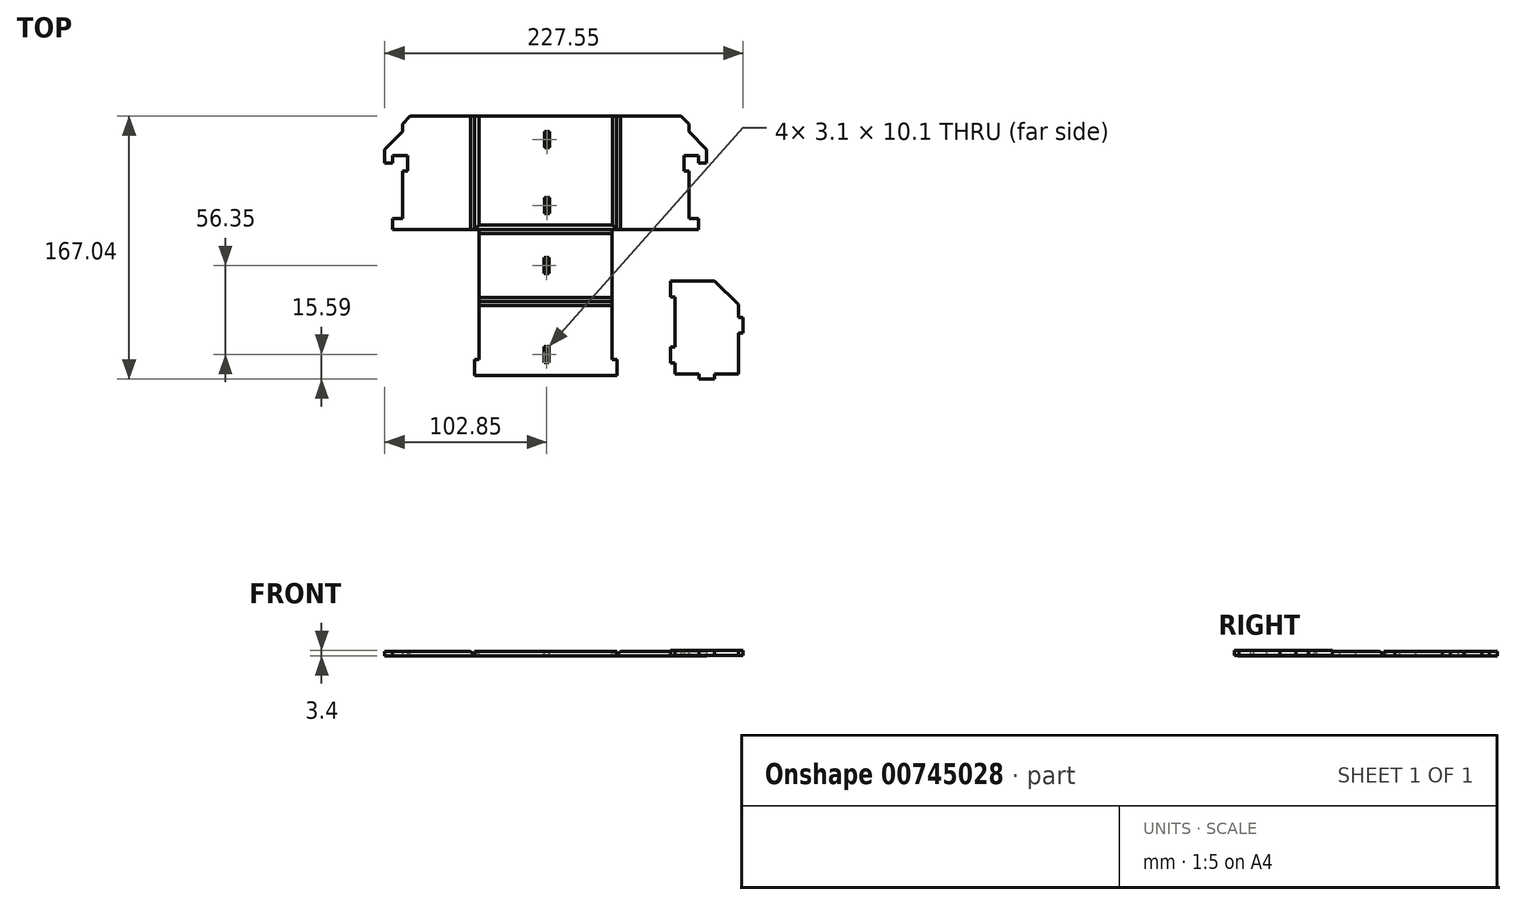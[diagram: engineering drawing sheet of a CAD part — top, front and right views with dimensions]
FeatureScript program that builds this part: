
annotation { "Feature Type Name" : "Feature", "Feature Type Description" : "" }
export const myFeature = defineFeature(function(context is Context, id is Id, definition is map)
    precondition{}
    {
        {
            var Q0;
            Q0=qCreatedBy(makeId("Top.planeOp"),FACE);
            var sketch = newSketch(context, id + "F0", { "sketchPlane" : qUnion([Q0])});
            skLineSegment(sketch, "E0.bottom", {"start": v(45, -36) * mm, "end": v(-45, -36) * mm});
            skLineSegment(sketch, "E0.top", {"start": v(45, 36) * mm, "end": v(-45, 36) * mm});
            skLineSegment(sketch, "E0.left", {"start": v(45, -36) * mm, "end": v(45, 36) * mm});
            skLineSegment(sketch, "E0.right", {"start": v(-45, -36) * mm, "end": v(-45, 36) * mm});
            skPoint(sketch, "E0.middle", {"position": v(0, 0) * mm});
            skLineSegment(sketch, "E1.bottom", {"start": v(45, 36) * mm, "end": v(91, 36) * mm});
            skLineSegment(sketch, "E1.top", {"start": v(45, -36) * mm, "end": v(91, -36) * mm});
            skLineSegment(sketch, "E1.left", {"start": v(45, 36) * mm, "end": v(45, -36) * mm});
            skLineSegment(sketch, "E1.right", {"start": v(91, 1) * mm, "end": v(91, -29) * mm});
            skLineSegment(sketch, "E2.bottom", {"start": v(-45, 36) * mm, "end": v(-91, 36) * mm});
            skLineSegment(sketch, "E2.top", {"start": v(-45, -36) * mm, "end": v(-91, -36) * mm});
            skLineSegment(sketch, "E2.left", {"start": v(-45, 36) * mm, "end": v(-45, -36) * mm});
            skLineSegment(sketch, "E2.right", {"start": v(-91, 36) * mm, "end": v(-91, 26) * mm});
            skLineSegment(sketch, "E3", {"start": v(91, 11) * mm, "end": v(97.2, 11) * mm});
            skLineSegment(sketch, "E4", {"start": v(97.2, 11) * mm, "end": v(97.2, 6) * mm});
            skLineSegment(sketch, "E5", {"start": v(97.2, 6) * mm, "end": v(102.2, 6) * mm});
            skPoint(sketch, "E6", {"position": v(102.2, 6) * mm});
            skLineSegment(sketch, "E7.bottom", {"start": v(91, -36) * mm, "end": v(97.2, -36) * mm});
            skLineSegment(sketch, "E7.top", {"start": v(91, -29) * mm, "end": v(97.2, -29) * mm});
            skLineSegment(sketch, "E7.right", {"start": v(97.2, -36) * mm, "end": v(97.2, -29) * mm});
            skLineSegment(sketch, "E8", {"start": v(91, 36) * mm, "end": v(91, 26) * mm});
            skLineSegment(sketch, "E9", {"start": v(91, 26) * mm, "end": v(102.2, 14.8) * mm});
            skLineSegment(sketch, "E10", {"start": v(102.2, 6) * mm, "end": v(102.2, 14.8) * mm});
            skLineSegment(sketch, "E11.MirrorCS", {"start": v(-91, 26) * mm, "end": v(-102.2, 14.8) * mm});
            skLineSegment(sketch, "E12.MirrorCS", {"start": v(-102.2, 6) * mm, "end": v(-102.2, 14.8) * mm});
            skLineSegment(sketch, "E13.MirrorCS", {"start": v(-97.2, 6) * mm, "end": v(-102.2, 6) * mm});
            skLineSegment(sketch, "E14.MirrorCS", {"start": v(-97.2, 11) * mm, "end": v(-97.2, 6) * mm});
            skLineSegment(sketch, "E15.MirrorCS", {"start": v(-91, 11) * mm, "end": v(-97.2, 11) * mm});
            skLineSegment(sketch, "E16.MirrorCS", {"start": v(-91, -29) * mm, "end": v(-97.2, -29) * mm});
            skLineSegment(sketch, "E17.MirrorCS", {"start": v(-97.2, -36) * mm, "end": v(-97.2, -29) * mm});
            skLineSegment(sketch, "E18.MirrorCS", {"start": v(-91, -36) * mm, "end": v(-97.2, -36) * mm});
            skLineSegment(sketch, "E19.trimOffspring", {"start": v(-91, 1) * mm, "end": v(-91, -29) * mm});
            skLineSegment(sketch, "E20.bottom", {"start": v(-42.2, -36) * mm, "end": v(42.2, -36) * mm});
            skLineSegment(sketch, "E20.top", {"start": v(-42.2, -81.8) * mm, "end": v(42.2, -81.8) * mm});
            skLineSegment(sketch, "E20.left", {"start": v(-42.2, -36) * mm, "end": v(-42.2, -81.8) * mm});
            skLineSegment(sketch, "E20.right", {"start": v(42.2, -36) * mm, "end": v(42.2, -81.8) * mm});
            skLineSegment(sketch, "E21.top", {"start": v(-42.2, -128.8) * mm, "end": v(42.2, -128.8) * mm});
            skLineSegment(sketch, "E21.left", {"start": v(-42.2, -81.8) * mm, "end": v(-42.2, -128.8) * mm});
            skLineSegment(sketch, "E21.right", {"start": v(42.2, -81.8) * mm, "end": v(42.2, -128.8) * mm});
            skLineSegment(sketch, "E22", {"start": v(91, 11) * mm, "end": v(87.8, 11) * mm});
            skLineSegment(sketch, "E23", {"start": v(87.8, 11) * mm, "end": v(87.8, 1) * mm});
            skLineSegment(sketch, "E24", {"start": v(87.8, 1) * mm, "end": v(91, 1) * mm});
            skLineSegment(sketch, "E25.MirrorCS", {"start": v(-91, 11) * mm, "end": v(-87.8, 11) * mm});
            skLineSegment(sketch, "E26.MirrorCS", {"start": v(-87.8, 11) * mm, "end": v(-87.8, 1) * mm});
            skLineSegment(sketch, "E27.MirrorCS", {"start": v(-87.8, 1) * mm, "end": v(-91, 1) * mm});
            skSolve(sketch);
        }
        {
            var Q0;
            Q0=makeQuery(id+"F0.imprint","IMPRINT",FACE,{"disambiguationData":[TD([[makeQuery(id+"F0.imprint","IMPRINT",EDGE,{"derivedFrom":sQuery(id+"F0.wireOp",EDGE,"E0.right")}),1.0]])]});
            var Q1;
            Q1=makeQuery(id+"F0.imprint","IMPRINT",FACE,{"disambiguationData":[TD([[makeQuery(id+"F0.imprint","IMPRINT",EDGE,{"derivedFrom":sQuery(id+"F0.wireOp",EDGE,"E0.left")}),-1.0]])]});
            extrude(context, id + "F1", {"entities" : qUnion([Q0, Q1]), "depth" : 2.6 * mm, "offsetDistance" : 25 * mm});
        }
        {
            var Q0;
            Q0=makeQuery(id+"F1.opExtrude","CAP_EDGE",EDGE,{"disambiguationData":[OSD([sQuery(id+"F0.wireOp",EDGE,"E0.left")])],"isStart":false});
            var Q1;
            Q1=makeQuery(id+"F1.opExtrude","CAP_EDGE",EDGE,{"disambiguationData":[OSD([sQuery(id+"F0.wireOp",EDGE,"E0.right")])],"isStart":false});
            chamfer(context, id + "F2", {"entities" : qUnion([Q0, Q1]), "width" : 2.6 * mm, "tangentPropagation" : true});
        }
        {
            var Q0;
            Q0=makeQuery(id+"F0.imprint","IMPRINT",FACE,{"disambiguationData":[TD([[makeQuery(id+"F0.imprint","IMPRINT",EDGE,{"derivedFrom":sQuery(id+"F0.wireOp",EDGE,"E0.top")}),1.0]])]});
            extrude(context, id + "F3", {"entities" : qUnion([Q0]), "depth" : 2.6 * mm, "offsetDistance" : 25 * mm});
        }
        {
            var Q0;
            Q0=makeQuery(id+"F3.opExtrude","CAP_EDGE",EDGE,{"disambiguationData":[OSD([sQuery(id+"F0.wireOp",EDGE,"E0.left")])],"isStart":false});
            var Q1;
            Q1=makeQuery(id+"F3.opExtrude","CAP_EDGE",EDGE,{"disambiguationData":[OSD([sQuery(id+"F0.wireOp",EDGE,"E0.right")])],"isStart":false});
            var Q2;
            Q2=makeQuery(id+"F3.opExtrude","CAP_EDGE",EDGE,{"disambiguationData":[OSD([sQuery(id+"F0.wireOp",EDGE,"E0.bottom")])],"isStart":false});
            chamfer(context, id + "F4", {"entities" : qUnion([Q0, Q1, Q2]), "width" : 2.6 * mm, "tangentPropagation" : true});
        }
        {
            var Q0;
            Q0=makeQuery(id+"F3.opExtrude","CAP_FACE",FACE,{"disambiguationData":[OSD([sQuery(id+"F0.wireOp",EDGE,"E0.bottom"),sQuery(id+"F0.wireOp",EDGE,"E0.top"),sQuery(id+"F0.wireOp",EDGE,"E0.left"),sQuery(id+"F0.wireOp",EDGE,"E0.right")])],"isStart":false});
            var sketch = newSketch(context, id + "F5", { "sketchPlane" : qUnion([Q0])});
            skLineSegment(sketch, "E28.bottom", {"start": v(-0.7, 26) * mm, "end": v(2.4, 26) * mm});
            skLineSegment(sketch, "E28.top", {"start": v(-0.7, 15.9) * mm, "end": v(2.4, 15.9) * mm});
            skLineSegment(sketch, "E28.left", {"start": v(-0.7, 26) * mm, "end": v(-0.7, 15.9) * mm});
            skLineSegment(sketch, "E28.right", {"start": v(2.4, 26) * mm, "end": v(2.4, 15.9) * mm});
            skLineSegment(sketch, "E29.bottom", {"start": v(-0.7, -15.9) * mm, "end": v(2.4, -15.9) * mm});
            skLineSegment(sketch, "E29.top", {"start": v(-0.7, -26) * mm, "end": v(2.4, -26) * mm});
            skLineSegment(sketch, "E29.left", {"start": v(-0.7, -15.9) * mm, "end": v(-0.7, -26) * mm});
            skLineSegment(sketch, "E29.right", {"start": v(2.4, -15.9) * mm, "end": v(2.4, -26) * mm});
            skSolve(sketch);
        }
        {
            var Q0;
            Q0=makeQuery(id+"F5.imprint","IMPRINT",FACE,{"disambiguationData":[TD([[makeQuery(id+"F5.imprint","IMPRINT",EDGE,{"derivedFrom":sQuery(id+"F5.wireOp",EDGE,"E28.bottom")}),-1.0]])]});
            var Q1;
            Q1=makeQuery(id+"F5.imprint","IMPRINT",FACE,{"disambiguationData":[TD([[makeQuery(id+"F5.imprint","IMPRINT",EDGE,{"derivedFrom":sQuery(id+"F5.wireOp",EDGE,"E29.bottom")}),-1.0]])]});
            extrude(context, id + "F6", {"entities" : qUnion([Q0, Q1]), "operationType" : NewBodyOperationType.REMOVE, "oppositeDirection" : true, "depth" : 4 * mm, "offsetDistance" : 25 * mm});
        }
        {
            var Q0;
            Q0=makeQuery(id+"F0.imprint","IMPRINT",FACE,{"disambiguationData":[TD([[makeQuery(id+"F0.imprint","IMPRINT",EDGE,{"derivedFrom":sQuery(id+"F0.wireOp",EDGE,"E20.top")}),1.0]])]});
            extrude(context, id + "F7", {"entities" : qUnion([Q0]), "depth" : 2.6 * mm, "offsetDistance" : 25 * mm});
        }
        {
            var Q0;
            Q0=makeQuery(id+"F7.opExtrude","CAP_EDGE",EDGE,{"disambiguationData":[OSD([sQuery(id+"F0.wireOp",EDGE,"E0.bottom")])],"isStart":false});
            var Q1;
            Q1=makeQuery(id+"F7.opExtrude","CAP_EDGE",EDGE,{"disambiguationData":[OSD([sQuery(id+"F0.wireOp",EDGE,"E20.top")])],"isStart":false});
            chamfer(context, id + "F8", {"entities" : qUnion([Q0, Q1]), "width" : 2.6 * mm, "tangentPropagation" : true});
        }
        {
            var Q0;
            Q0=makeQuery(id+"F0.imprint","IMPRINT",FACE,{"disambiguationData":[TD([[makeQuery(id+"F0.imprint","IMPRINT",EDGE,{"derivedFrom":sQuery(id+"F0.wireOp",EDGE,"E20.top")}),-1.0]])]});
            extrude(context, id + "F9", {"entities" : qUnion([Q0]), "depth" : 2.6 * mm, "offsetDistance" : 25 * mm});
        }
        {
            var Q0;
            Q0=makeQuery(id+"F9.opExtrude","CAP_EDGE",EDGE,{"disambiguationData":[OSD([sQuery(id+"F0.wireOp",EDGE,"E20.top")])],"isStart":false});
            chamfer(context, id + "F10", {"entities" : qUnion([Q0]), "width" : 2.6 * mm, "tangentPropagation" : true});
        }
        {
            var Q0;
            Q0=makeQuery(id+"F9.opExtrude","SWEPT_FACE",FACE,{"disambiguationData":[OSD([sQuery(id+"F0.wireOp",EDGE,"E21.left")])]});
            var sketch = newSketch(context, id + "F11", { "sketchPlane" : qUnion([Q0])});
            skLineSegment(sketch, "E30.bottom", {"start": v(128.8, -0.2) * mm, "end": v(118.8, -0.2) * mm});
            skLineSegment(sketch, "E30.top", {"start": v(128.8, 2.6) * mm, "end": v(118.8, 2.6) * mm});
            skLineSegment(sketch, "E30.left", {"start": v(128.8, -0.2) * mm, "end": v(128.8, 2.6) * mm});
            skLineSegment(sketch, "E30.right", {"start": v(118.8, -0.2) * mm, "end": v(118.8, 2.6) * mm});
            skSolve(sketch);
        }
        {
            var Q0;
            {var subQ0=sQuery(id+"F11.wireOp",EDGE,"E30.top");Q0=makeQuery(id+"F11.imprint","IMPRINT",FACE,{"disambiguationData":[TD([[makeQuery(id+"F11.imprint","IMPRINT",EDGE,{"derivedFrom":subQ0}),-1.0]])]});}
            extrude(context, id + "F12", {"entities" : qUnion([Q0]), "depth" : 3 * mm, "offsetDistance" : 25 * mm});
        }
        {
            var Q0;
            Q0=makeQuery(id+"F12.opExtrude","SWEPT_BODY",BODY,{"disambiguationData":[OSD([sQuery(id+"F11.wireOp",EDGE,"E30.bottom"),sQuery(id+"F11.wireOp",EDGE,"E30.top"),sQuery(id+"F11.wireOp",EDGE,"E30.left"),sQuery(id+"F11.wireOp",EDGE,"E30.right")])]});
            var Q1;
            Q1=qCreatedBy(makeId("Right.planeOp"),FACE);
            mirror(context, id + "F13", {"operationType" : NewBodyOperationType.ADD, "entities" : qUnion([Q0]), "mirrorPlane" : qUnion([Q1])});
        }
        {
            var Q0;
            Q0=makeQuery(id+"F7.opExtrude","CAP_FACE",FACE,{"disambiguationData":[OSD([sQuery(id+"F0.wireOp",EDGE,"E0.bottom"),sQuery(id+"F0.wireOp",EDGE,"E20.top"),sQuery(id+"F0.wireOp",EDGE,"E20.left"),sQuery(id+"F0.wireOp",EDGE,"E20.right")])],"isStart":false});
            var sketch = newSketch(context, id + "F14", { "sketchPlane" : qUnion([Q0])});
            skLineSegment(sketch, "E31.bottom", {"start": v(-0.9, -54.05) * mm, "end": v(2.2, -54.05) * mm});
            skLineSegment(sketch, "E31.top", {"start": v(-0.9, -64.15) * mm, "end": v(2.2, -64.15) * mm});
            skLineSegment(sketch, "E31.left", {"start": v(-0.9, -54.05) * mm, "end": v(-0.9, -64.15) * mm});
            skLineSegment(sketch, "E31.right", {"start": v(2.2, -54.05) * mm, "end": v(2.2, -64.15) * mm});
            skSolve(sketch);
        }
        {
            var Q0;
            {var subQ0=makeQuery(id+"F12.opExtrude","SWEPT_FACE",FACE,{"disambiguationData":[OSD([sQuery(id+"F11.wireOp",EDGE,"E30.top")])]});Q0=makeQuery(id+"F13.boolean.opBoolean","MERGE",FACE,{"derivedFrom":[makeQuery(id+"F9.opExtrude","CAP_FACE",FACE,{"disambiguationData":[OSD([sQuery(id+"F0.wireOp",EDGE,"E20.top"),sQuery(id+"F0.wireOp",EDGE,"E21.top"),sQuery(id+"F0.wireOp",EDGE,"E21.left"),sQuery(id+"F0.wireOp",EDGE,"E21.right")])],"isStart":false}),subQ0,makeQuery(id+"F13.opPattern","COPY",FACE,{"derivedFrom":subQ0,"instanceName":"1"})]});}
            var sketch = newSketch(context, id + "F15", { "sketchPlane" : qUnion([Q0])});
            skLineSegment(sketch, "E32.bottom", {"start": v(-0.9, -110.4) * mm, "end": v(2.2, -110.4) * mm});
            skLineSegment(sketch, "E32.top", {"start": v(-0.9, -120.5) * mm, "end": v(2.2, -120.5) * mm});
            skLineSegment(sketch, "E32.left", {"start": v(-0.9, -110.4) * mm, "end": v(-0.9, -120.5) * mm});
            skLineSegment(sketch, "E32.right", {"start": v(2.2, -110.4) * mm, "end": v(2.2, -120.5) * mm});
            skSolve(sketch);
        }
        {
            var Q0;
            Q0=makeQuery(id+"F15.imprint","IMPRINT",FACE,{"disambiguationData":[TD([[makeQuery(id+"F15.imprint","IMPRINT",EDGE,{"derivedFrom":sQuery(id+"F15.wireOp",EDGE,"E32.bottom")}),-1.0]])]});
            var Q1;
            Q1=makeQuery(id+"F14.imprint","IMPRINT",FACE,{"disambiguationData":[TD([[makeQuery(id+"F14.imprint","IMPRINT",EDGE,{"derivedFrom":sQuery(id+"F14.wireOp",EDGE,"E31.bottom")}),-1.0]])]});
            extrude(context, id + "F16", {"entities" : qUnion([Q0, Q1]), "operationType" : NewBodyOperationType.REMOVE, "oppositeDirection" : true, "depth" : 4 * mm, "offsetDistance" : 25 * mm});
        }
        {
            var Q0;
            Q0=qCreatedBy(makeId("Top.planeOp"),FACE);
            var sketch = newSketch(context, id + "F17", { "sketchPlane" : qUnion([Q0])});
            skLineSegment(sketch, "E33.bottom", {"start": v(82.15, -58.84) * mm, "end": v(122.35, -58.84) * mm});
            skLineSegment(sketch, "E33.top", {"start": v(82.15, -128.04) * mm, "end": v(97.25, -128.04) * mm});
            skLineSegment(sketch, "E33.left", {"start": v(82.15, -58.84) * mm, "end": v(82.15, -68.89) * mm});
            skLineSegment(sketch, "E33.right", {"start": v(122.35, -58.84) * mm, "end": v(122.35, -91.99) * mm});
            skPoint(sketch, "E34", {"position": v(82.15, -68.89) * mm});
            skLineSegment(sketch, "E35", {"start": v(82.15, -68.89) * mm, "end": v(79.15, -68.89) * mm});
            skLineSegment(sketch, "E36", {"start": v(79.15, -68.89) * mm, "end": v(79.15, -78.89) * mm});
            skLineSegment(sketch, "E37", {"start": v(79.15, -78.89) * mm, "end": v(82.15, -78.89) * mm});
            skLineSegment(sketch, "E38.trimOffspring", {"start": v(82.15, -78.89) * mm, "end": v(82.15, -110.79) * mm});
            skLineSegment(sketch, "E39", {"start": v(102.25, -131.04) * mm, "end": v(97.25, -131.04) * mm});
            skLineSegment(sketch, "E40", {"start": v(97.25, -131.04) * mm, "end": v(97.25, -128.04) * mm});
            skLineSegment(sketch, "E41", {"start": v(102.25, -131.04) * mm, "end": v(107.25, -131.04) * mm});
            skLineSegment(sketch, "E42", {"start": v(107.25, -131.04) * mm, "end": v(107.25, -128.04) * mm});
            skLineSegment(sketch, "E43.trimOffspring", {"start": v(107.25, -128.04) * mm, "end": v(122.35, -128.04) * mm});
            skLineSegment(sketch, "E44", {"start": v(82.15, -68.89) * mm, "end": v(122.35, -68.89) * mm});
            skPoint(sketch, "E45", {"position": v(122.35, -101.99) * mm});
            skLineSegment(sketch, "E46", {"start": v(122.35, -101.99) * mm, "end": v(125.35, -101.99) * mm});
            skLineSegment(sketch, "E47", {"start": v(125.35, -101.99) * mm, "end": v(125.35, -91.99) * mm});
            skLineSegment(sketch, "E48", {"start": v(125.35, -91.99) * mm, "end": v(122.35, -91.99) * mm});
            skLineSegment(sketch, "E49.trimOffspring", {"start": v(122.35, -101.99) * mm, "end": v(122.35, -128.04) * mm});
            skPoint(sketch, "E50", {"position": v(82.15, -110.79) * mm});
            skLineSegment(sketch, "E51", {"start": v(82.15, -110.79) * mm, "end": v(79.15, -110.79) * mm});
            skLineSegment(sketch, "E52", {"start": v(79.15, -110.79) * mm, "end": v(79.15, -120.79) * mm});
            skLineSegment(sketch, "E53", {"start": v(79.15, -120.79) * mm, "end": v(82.15, -120.79) * mm});
            skLineSegment(sketch, "E54.trimOffspring", {"start": v(82.15, -120.79) * mm, "end": v(82.15, -128.04) * mm});
            skSolve(sketch);
        }
        {
            var Q0;
            Q0=makeQuery(id+"F17.imprint","IMPRINT",FACE,{"disambiguationData":[TD([[makeQuery(id+"F17.imprint","IMPRINT",EDGE,{"derivedFrom":sQuery(id+"F17.wireOp",EDGE,"E33.top")}),1.0]])]});
            extrude(context, id + "F18", {"entities" : qUnion([Q0]), "depth" : 3 * mm, "offsetDistance" : 25 * mm});
        }
        {
            var Q0;
            Q0=makeQuery(id+"F1.opExtrude","SWEPT_EDGE",EDGE,{"disambiguationData":[OSD([sQuery(id+"F0.wireOp",EDGE,"E1.bottom"),sQuery(id+"F0.wireOp",EDGE,"E8")])]});
            var Q1;
            Q1=makeQuery(id+"F1.opExtrude","SWEPT_EDGE",EDGE,{"disambiguationData":[OSD([sQuery(id+"F0.wireOp",EDGE,"E2.bottom"),sQuery(id+"F0.wireOp",EDGE,"E2.right")])]});
            chamfer(context, id + "F19", {"entities" : qUnion([Q0, Q1]), "width" : 5 * mm, "tangentPropagation" : true});
        }
        {
            var Q0;
            Q0=makeQuery(id+"F18.opExtrude","SWEPT_EDGE",EDGE,{"disambiguationData":[OSD([sQuery(id+"F17.wireOp",EDGE,"E33.right"),sQuery(id+"F17.wireOp",EDGE,"E44")])]});
            chamfer(context, id + "F20", {"entities" : qUnion([Q0]), "width" : 15 * mm, "tangentPropagation" : true});
        }
        {
            var Q0;
            {var subQ4=sQuery(id+"F0.wireOp",EDGE,"E0.left");var subQ6=sQuery(id+"F0.wireOp",EDGE,"E0.right");var subQ10=makeQuery(id+"F0.imprint","IMPRINT",EDGE,{"derivedFrom":subQ4});var subQ11=makeQuery(id+"F0.imprint","IMPRINT",EDGE,{"derivedFrom":subQ6});var subQ12=makeQuery(id+"F0.imprint","IMPRINT",EDGE,{"derivedFrom":sQuery(id+"F0.wireOp",EDGE,"E20.top")});Q0=qUnion([makeQuery(id+"F0.imprint","IMPRINT",FACE,{"disambiguationData":[TD([[subQ10,-1.0]])]}),makeQuery(id+"F0.imprint","IMPRINT",FACE,{"disambiguationData":[TD([[subQ11,1.0]])]}),makeQuery(id+"F0.imprint","IMPRINT",FACE,{"disambiguationData":[TD([[subQ12,-1.0]])]}),makeQuery(id+"F0.imprint","IMPRINT",FACE,{"disambiguationData":[TD([[subQ12,1.0]])]}),makeQuery(id+"F0.imprint","IMPRINT",FACE,{"disambiguationData":[TD([[makeQuery(id+"F0.imprint","IMPRINT",EDGE,{"derivedFrom":sQuery(id+"F0.wireOp",EDGE,"E0.top")}),1.0]])]})]);}
            extrude(context, id + "F21", {"entities" : qUnion([Q0]), "operationType" : NewBodyOperationType.ADD, "oppositeDirection" : true, "depth" : 0.4 * mm, "offsetDistance" : 25 * mm});
        }
        {
            var Q0;
            {var subQ2=sQuery(id+"F0.wireOp",EDGE,"E20.right");var subQ3=sQuery(id+"F0.wireOp",EDGE,"E21.right");var subQ4=sQuery(id+"F0.wireOp",EDGE,"E21.top");var subQ6=sQuery(id+"F0.wireOp",EDGE,"E21.left");var subQ7=makeQuery(id+"F12.opExtrude","SWEPT_FACE",FACE,{"disambiguationData":[OSD([subQ6])]});Q0=makeQuery(id+"F21.boolean.opBoolean","SPLIT",FACE,{"disambiguationData":[TD([makeQuery(id+"F7.opExtrude","SWEPT_FACE",FACE,{"disambiguationData":[OSD([subQ2])]})])],"derivedFrom":makeQuery(id+"F13.boolean.opBoolean","MERGE",FACE,{"derivedFrom":[makeQuery(id+"F9.opExtrude","CAP_FACE",FACE,{"disambiguationData":[OSD([sQuery(id+"F0.wireOp",EDGE,"E20.top"),subQ4,subQ6,subQ3])],"isStart":true}),subQ7,makeQuery(id+"F13.opPattern","COPY",FACE,{"derivedFrom":subQ7,"instanceName":"1"})]})});}
            var Q1;
            {var subQ2=sQuery(id+"F0.wireOp",EDGE,"E21.left");var subQ3=sQuery(id+"F0.wireOp",EDGE,"E20.left");var subQ4=sQuery(id+"F0.wireOp",EDGE,"E21.top");var subQ6=makeQuery(id+"F12.opExtrude","SWEPT_FACE",FACE,{"disambiguationData":[OSD([subQ2])]});Q1=makeQuery(id+"F21.boolean.opBoolean","SPLIT",FACE,{"disambiguationData":[TD([makeQuery(id+"F7.opExtrude","SWEPT_FACE",FACE,{"disambiguationData":[OSD([subQ3])]})])],"derivedFrom":makeQuery(id+"F13.boolean.opBoolean","MERGE",FACE,{"derivedFrom":[makeQuery(id+"F9.opExtrude","CAP_FACE",FACE,{"disambiguationData":[OSD([sQuery(id+"F0.wireOp",EDGE,"E20.top"),subQ4,subQ2,sQuery(id+"F0.wireOp",EDGE,"E21.right")])],"isStart":true}),subQ6,makeQuery(id+"F13.opPattern","COPY",FACE,{"derivedFrom":subQ6,"instanceName":"1"})]})});}
            extrude(context, id + "F22", {"entities" : qUnion([Q0, Q1]), "operationType" : NewBodyOperationType.ADD, "depth" : 0.4 * mm, "offsetDistance" : 25 * mm});
        }
        {
            var Q0;
            Q0 = qSketchRegion(id + "F15", true);
            var Q1;
            Q1 = qSketchRegion(id + "F14", true);
            var Q2;
            Q2 = qSketchRegion(id + "F5", true);
            extrude(context, id + "F23", {"entities" : qUnion([Q0, Q1, Q2]), "operationType" : NewBodyOperationType.REMOVE, "oppositeDirection" : true, "depth" : 25 * mm, "offsetDistance" : 25 * mm});
        }
        {
            var Q0;
            Q0=makeQuery(id+"F21.opExtrude","SWEPT_EDGE",EDGE,{"disambiguationData":[OSD([sQuery(id+"F0.wireOp",EDGE,"E2.bottom"),sQuery(id+"F0.wireOp",EDGE,"E2.right")])]});
            var Q1;
            Q1=makeQuery(id+"F21.opExtrude","SWEPT_EDGE",EDGE,{"disambiguationData":[OSD([sQuery(id+"F0.wireOp",EDGE,"E1.bottom"),sQuery(id+"F0.wireOp",EDGE,"E8")])]});
            chamfer(context, id + "F24", {"entities" : qUnion([Q0, Q1]), "width" : 5 * mm, "tangentPropagation" : true});
        }
    });
